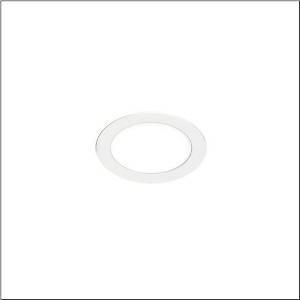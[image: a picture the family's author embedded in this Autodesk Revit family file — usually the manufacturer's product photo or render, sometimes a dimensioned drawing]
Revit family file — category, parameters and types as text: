
# Revit family: lunis_41_flat_51dr10ddgbb
name_source: partatom
category: Lighting Fixtures
units: mm (PartAtom-declared; Revit-internal decimal feet)

## family parameters
Cut with Voids When Loaded = No
Host = Face
Light Source = No
Part Type = Normal
Room Calculation Point = No
Round Connector Dimension = Use Diameter
Shared = No

## types (1)
- --- (1 x LED, 1750 lm, 14 W, 4000K)
    Apparent Load = 14 VA
    CIE Flux Codes = 49 80 96 100 100
    Color Rendering = 80
    Color Temperature = 4000K
    Default Elevation = 1800 mm
    Description = Lunis 41 Flat, downlight, light emission: direct distribution, LED rated luminous flux: 1.750lm, light colour: 830/840, control gear: ECG, mains connection: 230V, AC, 50/60Hz, housing, round, of aluminium, coated, traffic white (RAL 9016), diameter: 170mm, protection rating (complete): IP20, protection rating (on room side): IP44, insulation class (complete): insulation class II (safety insulation), certification: CE, permissible ambient temperature for indoor applications: -20..+40°C, packaging unit: 1 piece
    Height = 0 mm  [stored 0 ft]
    Lamp = 1 x LED
    Lamp Light Flux = 1750 lm
    Lamp Power = 14 W
    Lamp count = 1
    Length = 170 mm  [stored 0.557743 ft]
    Luminous efficacy = 125 lm/W
    Manufacturer = Siteco
    ModVariant = No
    Model = 51DR10DDGBB
    Mounting Place = Ceiling
    Mounting Type = Recessed
    Number of Poles = 1
    OnlyDefault = Yes
    Power Factor = 1
    Product Name = Lunis 41 Flat
    Product group = downlight
    ProductGroupID = 401
    Protection Class = Protection class II
    Protection Degree = IP 20
    RLX_Detail_Level = 1
    RLX_Emergency_Light_Flux = 0 lm
    RLX_Emergency_Type = 0
    RLX_Emergency_Type_DB = No
    RlxData = <blob elided: 10869 chars, md5=fec630e2>
    Socket = socket
    Standby Power = 0 W
    System Light Flux = 1750 lm
    System Power = 14 W
    Type Comments = factory setting: colour temperature 4000K, luminous flux: 100 % | (ON | ON) | 350 mA
    Type Image = l_1340921.jpg
    URL = http://relux.com
    VarID = @adj_020013
    Voltage = 0 V
    Weight = 0.00 kg
    Width = 0 mm  [stored 0 ft]

note: [stored X ft] marks values corroborated as IEEE doubles in the binary element streams (Revit-internal decimal feet)

## geometry (parser evidence)
native form markers: Sweep x12
no freeform markers — native parametric forms only
